# Revit family: Fireplace_Gas_Heatilator_Courtyard
name_source: partatom
category: Mechanical Equipment
revit_build: Autodesk Revit 2015 (Build: 20140606_1530(x64)
units: mm (PartAtom-declared; Revit-internal decimal feet)

## types (4) — shared parameters
Assembly Code = D3020
Construction Details = http://www.arcat.com
Default Elevation = 0' - 0"
Door Width = 3' - 8"
DoorHeight = 2' - 6 1/2"
Efficiency Ratings = as Specified
Exhaust Connection Diameter = 9"
Fixture Finish = Metal - HHT - Metallic Black
Fuel Consumption = as Specified
HVAC_BTU Input = 0.0 Btu/h
HVAC_BTU Output = 0.0 Btu/h
Heating Capacity = as Specified
Keynote = 10305
Manufacturer = Heatilator
Manufacturer Website = http://www.heatilator.com
Opening Height = 2' - 6 3/4"
Opening Offset = 0' - 1 7/8"
Product Data = http://www.arcat.com
Revision = R1_2018-05
Sales Information = http://www.heatilator.com
Send Message = http://www.arcat.com
Specification = http://www.arcat.com
Standards Conformance = cULus  ;  ANSI Z21.97-2010  ;  CR97-003
URL = http://www.heatilator.com
Unit Depth = 1' - 5 1/2"
Unit Height = 3' - 8"
zero-valued in all types: Expected Lifespan (Years), Maintenance Schedule (Months), Unit Weight, Warranty Duration (Years)

## per-type parameters (varying)
| type | Description | Fuel Type | Model | Opening Width | Rear Width | Unit Width |
| 36 x 31 Viewing Area NG | Heatilator Outdoor Gas Burning Fireplace - Courtyard 36 as Specified | Natural Gas | ODCOUG-36 | 3' - 0" | 2' - 7 1/2" | 3' - 5 3/4" |
| 36 x 31 Viewing Area LP | Heatilator Outdoor Gas Burning Fireplace - Courtyard 36 as Specified | Liquid Petroleum | ODCOUG-36 | 3' - 0" | 2' - 7 1/2" | 3' - 5 3/4" |
| 42 x 31 Viewing Area NG | Heatilator Outdoor Gas Burning Fireplace - Courtyard 42 as Specified | Natural Gas | ODCOUG-42 | 3' - 6" | 3' - 1 1/2" | 3' - 11 3/4" |
| 42 x 31 Viewing Area LP | Heatilator Outdoor Gas Burning Fireplace - Courtyard 42 as Specified | Liquid Petroleum | ODCOUG-42 | 3' - 6" | 3' - 1 1/2" | 3' - 11 3/4" |

## geometry (parser evidence)
native form markers: Sweep x3
no freeform markers — native parametric forms only
